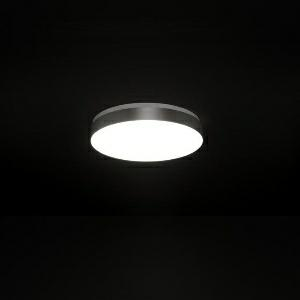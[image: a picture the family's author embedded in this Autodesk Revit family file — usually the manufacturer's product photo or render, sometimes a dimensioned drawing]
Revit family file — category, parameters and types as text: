
# Revit family: spectral_norea_norea-ra_306_1900_840_mps_4fb9
name_source: partatom
category: Lighting Fixtures
revit_build: Autodesk Revit 2016 (Build: 20150220_1215(x64)
units: mm (PartAtom-declared; Revit-internal decimal feet)

## family parameters
Cut with Voids When Loaded = No
Host = Face
Light Source = No
Part Type = Normal
Room Calculation Point = No
Round Connector Dimension = Use Diameter
Shared = No

## types (1)
- SPECTRAL NOREA (1 x )
    Apparent Load = 0 VA
    Approval mark = CE
    CIE Flux Codes = 73 93 98 100 62
    Control Gear = Electronic transformer
    Default Elevation = 1800 mm
    Description = SPT0000146
NOREA surface-mounted luminaire

Design:
Round luminaire element with a microprism panel in a natural anodised aluminium profile frame surround. The frame is fixed at the powder-coated metal body by a bayonet fixture with spring clip. The metal body accommodates the electrical components and electronic ballast. The LED module is formed as a round LED flat board and can be removed for mounting or exchange using a keyhole screw connection. Plug-in electrical connection of the LED flat board. Luminaire with heat-resistant wiring. Variant suitable for office use with a microprism panel MPS. The LED points are visible as circles on the microprism panel. Suitable for ceiling or wall mounting. Also in a dimmable version. Protection rating IP20, safety class I

Colour:
Housing – similar to RAL 9016 White silk matt;
Frame – natural anodised
    Height = 78 mm  [stored 0.255906 ft]
    Lamp = 1 x
    Lamp count = 1
    Length = 306 mm
    Luminous efficacy = 0 lm/W
    Manufacturer = Ridi
    ModVariant = No
    Model = NOREA-RA 306/1900/840 MPS
    Mounting Place = Ceiling
    Mounting Type = Surface mounted
    Number of Poles = 1
    OnlyDefault = Yes
    Power Factor = 1
    Product Name = SPECTRAL NOREA
    Product group = Ceiling mounted luminaire
    ProductGroupID = 3
    Protection Class = Protection class
    Protection Degree = IP 20
    RlxData = <blob elided: 30125 chars, md5=d183dc23>
    Socket = socket
    Standby Power = 0 W
    System Light Flux = 0 lm
    System Power = 0 W
    Type Image = rundmittel01_-_kopie.jpg
    URL = http://reluxnet.relux.com
    VarID = 1
    Voltage = 0 V
    Weight = 0.00 kg
    Width = 0 mm  [stored 0 ft]

note: [stored X ft] marks values corroborated as IEEE doubles in the binary element streams (Revit-internal decimal feet)

## geometry (parser evidence)
native form markers: Sweep x13
no freeform markers — native parametric forms only
